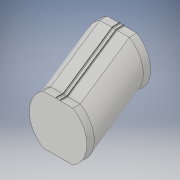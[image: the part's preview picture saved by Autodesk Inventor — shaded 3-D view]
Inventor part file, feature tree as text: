
AUTODESK INVENTOR PART (.ipt)
format: ipt  version: 2017 (Build 210142000, 142)  size: 195,584 bytes
history: native  units: in
note: dims shown in document units (in); Inventor stores cm internally (conversion verified against a paired STEP export)
features: sketch x2, extrude x2, plane x1, sweep x1
ambient origin geometry x8: Origin, YZ Plane, XZ Plane, XY Plane, X Axis, Y Axis, Z Axis, Center Point
bodies: Solid1 (feature_tree)
feature tree (6):
  sketch  "Sketch1"  dims[d0=6.6667in d3=1.0in d4=0.0in d12=8.0in]
  extrude  "connection top"  Depth=8.0in
  plane  "Work Plane2"
  sweep  "ramp"
  extrude  "connection bottom"  Depth=0.0892in TaperAngle=0.0deg
  sketch  "Sketch6"  dims[d28=8.0in d45=0.0in d46=0.0in d49=1.0in d50=0.0in d70=0.8521in d87=4.0in d88=0.5833in d89=3.8873in d90=3.8873in d91=1.7083in d92=0.0625in d93=0.0625in d94=1.6458in d95=0.25in d96=0.125in d97=0.0892in d98=0.0884in d99=45.0deg d100=3.3333in d101=0.125in d102=4.0in d103=0.5833in d104=3.8873in d105=3.8873in d106=1.7083in d107=0.0625in d108=0.0625in d109=1.6458in d110=0.25in d111=0.125in d112=0.0892in d113=0.0884in d114=45.0deg d115=3.3333in d116=0.125in]
